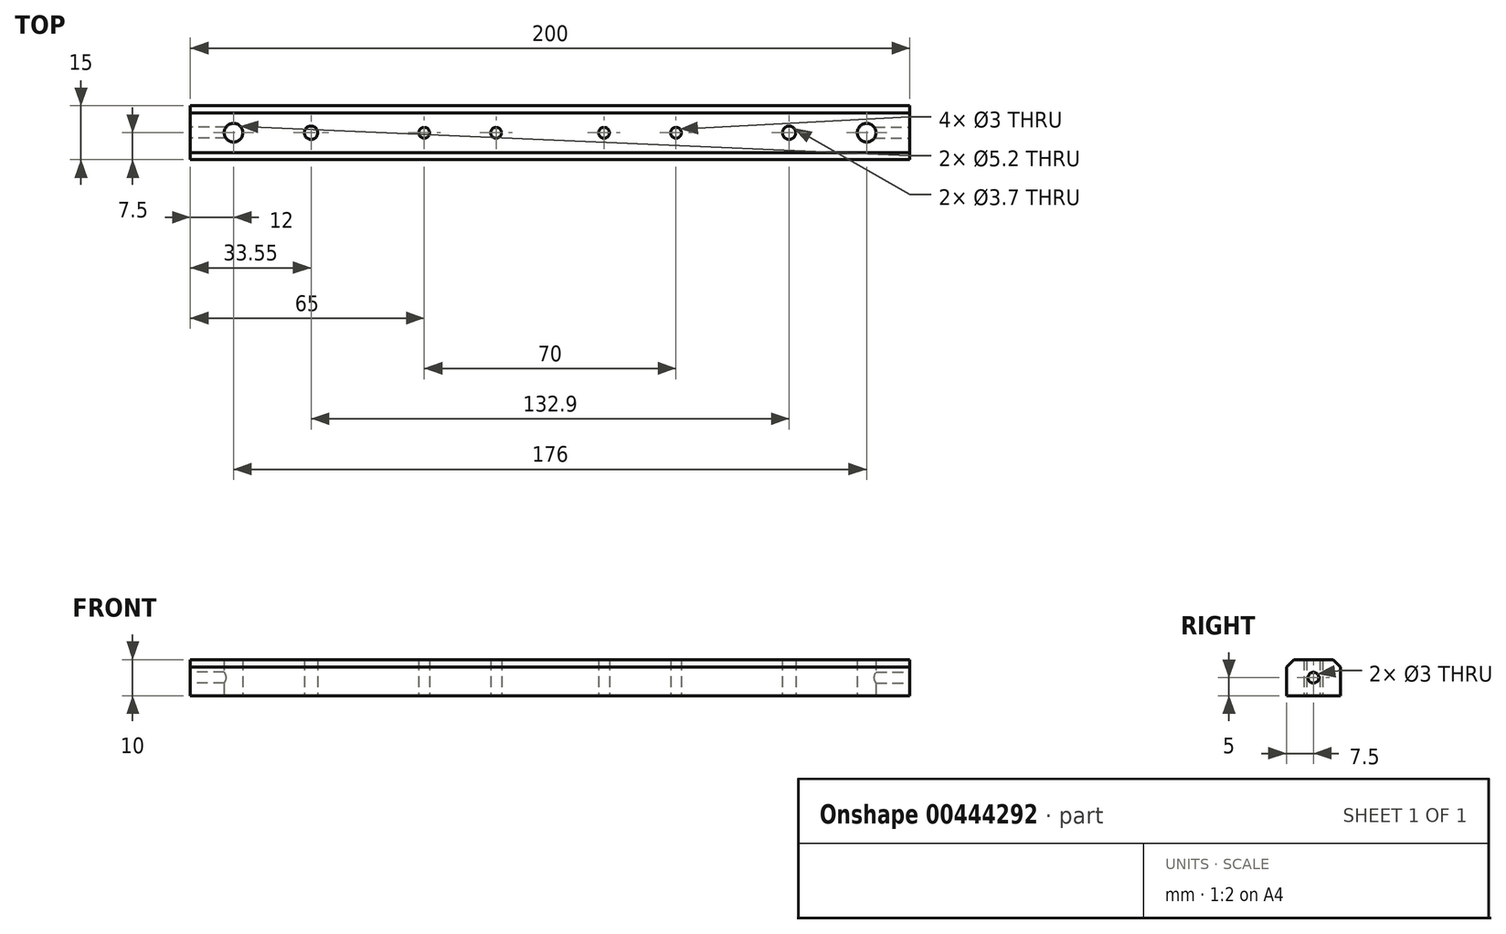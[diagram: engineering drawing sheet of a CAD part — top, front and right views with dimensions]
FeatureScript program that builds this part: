
annotation { "Feature Type Name" : "Feature", "Feature Type Description" : "" }
export const myFeature = defineFeature(function(context is Context, id is Id, definition is map)
    precondition{}
    {
        {
            var Q0;
            Q0=qCreatedBy(makeId("Top.planeOp"),FACE);
            var sketch = newSketch(context, id + "F0", { "sketchPlane" : qUnion([Q0])});
            skLineSegment(sketch, "E0.bottom", {"start": v(100, -7.5) * mm, "end": v(-100, -7.5) * mm});
            skLineSegment(sketch, "E0.top", {"start": v(100, 7.5) * mm, "end": v(-100, 7.5) * mm});
            skLineSegment(sketch, "E0.left", {"start": v(100, -7.5) * mm, "end": v(100, 7.5) * mm});
            skLineSegment(sketch, "E0.right", {"start": v(-100, -7.5) * mm, "end": v(-100, 7.5) * mm});
            skPoint(sketch, "E0.middle", {"position": v(0, 0) * mm});
            skCircle(sketch, "E1", {"center": v(-35, 0) * mm, "radius": 1.5 * mm});
            skCircle(sketch, "E2", {"center": v(-15, 0) * mm, "radius": 1.5 * mm});
            skCircle(sketch, "E3.MirrorC", {"center": v(15, 0) * mm, "radius": 1.5 * mm});
            skCircle(sketch, "E4.MirrorC", {"center": v(35, 0) * mm, "radius": 1.5 * mm});
            skCircle(sketch, "E5", {"center": v(-88, 0) * mm, "radius": 2.6 * mm});
            skCircle(sketch, "E6.MirrorC", {"center": v(88, 0) * mm, "radius": 2.6 * mm});
            skCircle(sketch, "E7", {"center": v(-66.45, 0) * mm, "radius": 1.85 * mm});
            skCircle(sketch, "E8.MirrorC", {"center": v(66.45, 0) * mm, "radius": 1.85 * mm});
            skSolve(sketch);
        }
        {
            var Q0;
            Q0 = qSketchRegion(id + "F0", true);
            extrude(context, id + "F1", {"entities" : qUnion([Q0]), "depth" : 10 * mm});
        }
        {
            var Q0;
            Q0=makeQuery(id+"F1.opExtrude","CAP_EDGE",EDGE,{"disambiguationData":[OSD([sQuery(id+"F0.wireOp",EDGE,"E0.top")])],"isStart":false});
            var Q1;
            Q1=makeQuery(id+"F1.opExtrude","CAP_EDGE",EDGE,{"disambiguationData":[OSD([sQuery(id+"F0.wireOp",EDGE,"E0.bottom")])],"isStart":false});
            chamfer(context, id + "F2", {"entities" : qUnion([Q0, Q1]), "width" : 2 * mm, "tangentPropagation" : true});
        }
        {
            var Q0;
            Q0=makeQuery(id+"F1.opExtrude","SWEPT_FACE",FACE,{"disambiguationData":[OSD([sQuery(id+"F0.wireOp",EDGE,"E0.right")])]});
            var sketch = newSketch(context, id + "F3", { "sketchPlane" : qUnion([Q0])});
            skCircle(sketch, "E9", {"center": v(0, 5) * mm, "radius": 1.5 * mm});
            skSolve(sketch);
        }
        {
            var Q0;
            Q0 = qSketchRegion(id + "F3", true);
            extrude(context, id + "F4", {"entities" : qUnion([Q0]), "operationType" : NewBodyOperationType.REMOVE, "oppositeDirection" : true, "depth" : 10 * mm});
        }
        {
            var Q0;
            Q0=makeQuery(id+"F1.opExtrude","SWEPT_FACE",FACE,{"disambiguationData":[OSD([sQuery(id+"F0.wireOp",EDGE,"E0.left")])]});
            var sketch = newSketch(context, id + "F5", { "sketchPlane" : qUnion([Q0])});
            skCircle(sketch, "E10", {"center": v(0, 5) * mm, "radius": 1.5 * mm});
            skSolve(sketch);
        }
        {
            var Q0;
            Q0 = qSketchRegion(id + "F5", true);
            extrude(context, id + "F6", {"entities" : qUnion([Q0]), "operationType" : NewBodyOperationType.REMOVE, "oppositeDirection" : true, "depth" : 10 * mm});
        }
    });
